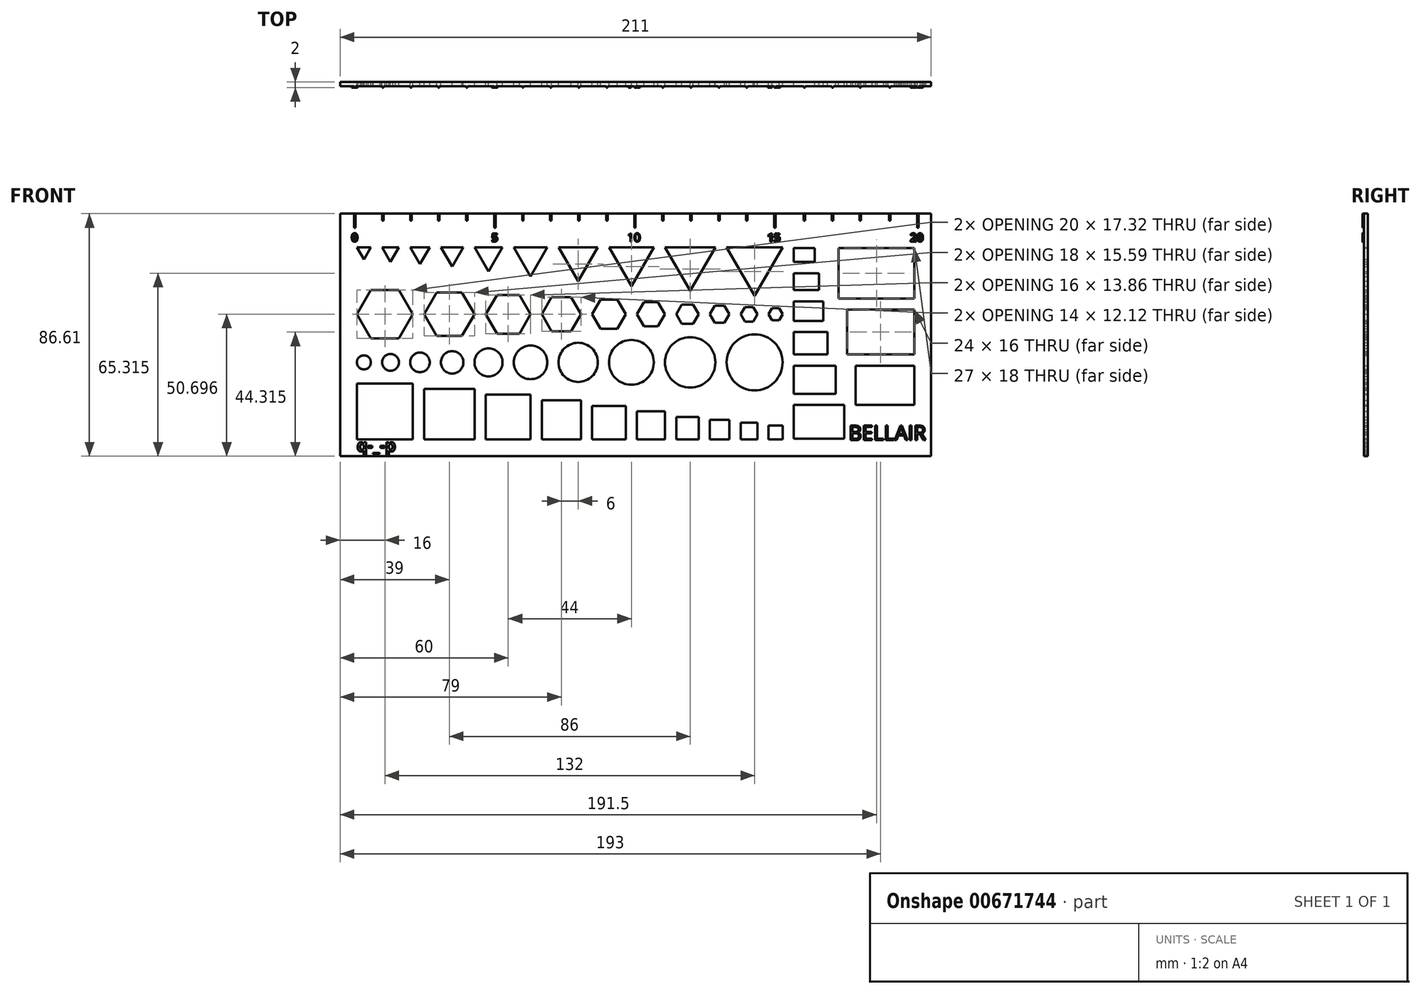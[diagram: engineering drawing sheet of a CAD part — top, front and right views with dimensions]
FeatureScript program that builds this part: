
annotation { "Feature Type Name" : "Feature", "Feature Type Description" : "" }
export const myFeature = defineFeature(function(context is Context, id is Id, definition is map)
    precondition{}
    {
        {
            var Q0;
            Q0=qCreatedBy(makeId("Front.planeOp"),FACE);
            var sketch = newSketch(context, id + "F0", { "sketchPlane" : qUnion([Q0])});
            skLineSegment(sketch, "E0.bottom", {"start": v(0, 0) * mm, "end": v(20, 0) * mm});
            skLineSegment(sketch, "E0.top", {"start": v(0, 20) * mm, "end": v(20, 20) * mm});
            skLineSegment(sketch, "E0.left", {"start": v(0, 0) * mm, "end": v(0, 20) * mm});
            skLineSegment(sketch, "E0.right", {"start": v(20, 0) * mm, "end": v(20, 20) * mm});
            skLineSegment(sketch, "E1.bottom", {"start": v(24, 0) * mm, "end": v(42, 0) * mm});
            skLineSegment(sketch, "E1.top", {"start": v(24, 18) * mm, "end": v(42, 18) * mm});
            skLineSegment(sketch, "E1.left", {"start": v(24, 0) * mm, "end": v(24, 18) * mm});
            skLineSegment(sketch, "E1.right", {"start": v(42, 0) * mm, "end": v(42, 18) * mm});
            skLineSegment(sketch, "E2.bottom", {"start": v(46, 0) * mm, "end": v(62, 0) * mm});
            skLineSegment(sketch, "E2.top", {"start": v(46, 16) * mm, "end": v(62, 16) * mm});
            skLineSegment(sketch, "E2.left", {"start": v(46, 0) * mm, "end": v(46, 16) * mm});
            skLineSegment(sketch, "E2.right", {"start": v(62, 0) * mm, "end": v(62, 16) * mm});
            skLineSegment(sketch, "E3.bottom", {"start": v(66, 0) * mm, "end": v(80, 0) * mm});
            skLineSegment(sketch, "E3.top", {"start": v(66, 14) * mm, "end": v(80, 14) * mm});
            skLineSegment(sketch, "E3.left", {"start": v(66, 0) * mm, "end": v(66, 14) * mm});
            skLineSegment(sketch, "E3.right", {"start": v(80, 0) * mm, "end": v(80, 14) * mm});
            skLineSegment(sketch, "E4.bottom", {"start": v(84, 0) * mm, "end": v(96, 0) * mm});
            skLineSegment(sketch, "E4.top", {"start": v(84, 12) * mm, "end": v(96, 12) * mm});
            skLineSegment(sketch, "E4.left", {"start": v(84, 0) * mm, "end": v(84, 12) * mm});
            skLineSegment(sketch, "E4.right", {"start": v(96, 0) * mm, "end": v(96, 12) * mm});
            skLineSegment(sketch, "E5.bottom", {"start": v(100, 0) * mm, "end": v(110, 0) * mm});
            skLineSegment(sketch, "E5.top", {"start": v(100, 10) * mm, "end": v(110, 10) * mm});
            skLineSegment(sketch, "E5.left", {"start": v(100, 0) * mm, "end": v(100, 10) * mm});
            skLineSegment(sketch, "E5.right", {"start": v(110, 0) * mm, "end": v(110, 10) * mm});
            skLineSegment(sketch, "E6.bottom", {"start": v(114, 0) * mm, "end": v(122, 0) * mm});
            skLineSegment(sketch, "E6.top", {"start": v(114, 8) * mm, "end": v(122, 8) * mm});
            skLineSegment(sketch, "E6.left", {"start": v(114, 0) * mm, "end": v(114, 8) * mm});
            skLineSegment(sketch, "E6.right", {"start": v(122, 0) * mm, "end": v(122, 8) * mm});
            skLineSegment(sketch, "E7.bottom", {"start": v(126, 0) * mm, "end": v(133, 0) * mm});
            skLineSegment(sketch, "E7.top", {"start": v(126, 7) * mm, "end": v(133, 7) * mm});
            skLineSegment(sketch, "E7.left", {"start": v(126, 0) * mm, "end": v(126, 7) * mm});
            skLineSegment(sketch, "E7.right", {"start": v(133, 0) * mm, "end": v(133, 7) * mm});
            skLineSegment(sketch, "E8.bottom", {"start": v(137, 0) * mm, "end": v(143, 0) * mm});
            skLineSegment(sketch, "E8.top", {"start": v(137, 6) * mm, "end": v(143, 6) * mm});
            skLineSegment(sketch, "E8.left", {"start": v(137, 0) * mm, "end": v(137, 6) * mm});
            skLineSegment(sketch, "E8.right", {"start": v(143, 0) * mm, "end": v(143, 6) * mm});
            skLineSegment(sketch, "E9.bottom", {"start": v(147, 0) * mm, "end": v(152, 0) * mm});
            skLineSegment(sketch, "E9.top", {"start": v(147, 5) * mm, "end": v(152, 5) * mm});
            skLineSegment(sketch, "E9.left", {"start": v(147, 0) * mm, "end": v(147, 5) * mm});
            skLineSegment(sketch, "E9.right", {"start": v(152, 0) * mm, "end": v(152, 5) * mm});
            skCircle(sketch, "E10", {"center": v(2.5, 27.5) * mm, "radius": 2.5 * mm});
            skCircle(sketch, "E11", {"center": v(12, 27.5) * mm, "radius": 3 * mm});
            skCircle(sketch, "E12", {"center": v(22.5, 27.5) * mm, "radius": 3.5 * mm});
            skCircle(sketch, "E13", {"center": v(34, 27.5) * mm, "radius": 4 * mm});
            skCircle(sketch, "E14", {"center": v(47, 27.5) * mm, "radius": 5 * mm});
            skCircle(sketch, "E15", {"center": v(62, 27.5) * mm, "radius": 6 * mm});
            skCircle(sketch, "E16", {"center": v(79, 27.5) * mm, "radius": 7 * mm});
            skCircle(sketch, "E17", {"center": v(98, 27.5) * mm, "radius": 8 * mm});
            skCircle(sketch, "E18", {"center": v(119, 27.5) * mm, "radius": 9 * mm});
            skCircle(sketch, "E19", {"center": v(142, 27.5) * mm, "radius": 10 * mm});
            skCircle(sketch, "E20.cCircle", {"center": v(10, 44.7) * mm, "radius": 8.66 * mm, "construction": true});
            skLineSegment(sketch, "E20.0", {"start": v(5, 53.36) * mm, "end": v(15, 53.36) * mm});
            skLineSegment(sketch, "E20.1", {"start": v(15, 53.36) * mm, "end": v(20, 44.7) * mm});
            skLineSegment(sketch, "E20.2", {"start": v(20, 44.7) * mm, "end": v(15, 36.04) * mm});
            skLineSegment(sketch, "E20.3", {"start": v(15, 36.04) * mm, "end": v(5, 36.04) * mm});
            skLineSegment(sketch, "E20.4", {"start": v(5, 36.04) * mm, "end": v(0, 44.7) * mm});
            skLineSegment(sketch, "E20.5", {"start": v(0, 44.7) * mm, "end": v(5, 53.36) * mm});
            skPoint(sketch, "E20.0.midPoint", {"position": v(10, 53.36) * mm});
            skCircle(sketch, "E21.cCircle", {"center": v(33, 44.7) * mm, "radius": 7.8 * mm, "construction": true});
            skLineSegment(sketch, "E21.0", {"start": v(37.5, 36.9) * mm, "end": v(28.5, 36.9) * mm});
            skLineSegment(sketch, "E21.1", {"start": v(28.5, 36.9) * mm, "end": v(24, 44.7) * mm});
            skLineSegment(sketch, "E21.2", {"start": v(24, 44.7) * mm, "end": v(28.5, 52.5) * mm});
            skLineSegment(sketch, "E21.3", {"start": v(28.5, 52.5) * mm, "end": v(37.5, 52.5) * mm});
            skLineSegment(sketch, "E21.4", {"start": v(37.5, 52.5) * mm, "end": v(42, 44.7) * mm});
            skLineSegment(sketch, "E21.5", {"start": v(42, 44.7) * mm, "end": v(37.5, 36.9) * mm});
            skPoint(sketch, "E21.0.midPoint", {"position": v(33, 36.9) * mm});
            skCircle(sketch, "E22.cCircle", {"center": v(54, 44.7) * mm, "radius": 6.93 * mm, "construction": true});
            skLineSegment(sketch, "E22.0", {"start": v(50, 51.62) * mm, "end": v(58, 51.62) * mm});
            skLineSegment(sketch, "E22.1", {"start": v(58, 51.62) * mm, "end": v(62, 44.7) * mm});
            skLineSegment(sketch, "E22.2", {"start": v(62, 44.7) * mm, "end": v(58, 37.77) * mm});
            skLineSegment(sketch, "E22.3", {"start": v(58, 37.77) * mm, "end": v(50, 37.77) * mm});
            skLineSegment(sketch, "E22.4", {"start": v(50, 37.77) * mm, "end": v(46, 44.7) * mm});
            skLineSegment(sketch, "E22.5", {"start": v(46, 44.7) * mm, "end": v(50, 51.62) * mm});
            skPoint(sketch, "E22.0.midPoint", {"position": v(54, 51.62) * mm});
            skCircle(sketch, "E23.cCircle", {"center": v(73, 44.7) * mm, "radius": 6.06 * mm, "construction": true});
            skLineSegment(sketch, "E23.0", {"start": v(69.5, 50.76) * mm, "end": v(76.5, 50.76) * mm});
            skLineSegment(sketch, "E23.1", {"start": v(76.5, 50.76) * mm, "end": v(80, 44.7) * mm});
            skLineSegment(sketch, "E23.2", {"start": v(80, 44.7) * mm, "end": v(76.5, 38.63) * mm});
            skLineSegment(sketch, "E23.3", {"start": v(76.5, 38.63) * mm, "end": v(69.5, 38.63) * mm});
            skLineSegment(sketch, "E23.4", {"start": v(69.5, 38.63) * mm, "end": v(66, 44.7) * mm});
            skLineSegment(sketch, "E23.5", {"start": v(66, 44.7) * mm, "end": v(69.5, 50.76) * mm});
            skPoint(sketch, "E23.0.midPoint", {"position": v(73, 50.76) * mm});
            skCircle(sketch, "E24.cCircle", {"center": v(90, 44.7) * mm, "radius": 5.2 * mm, "construction": true});
            skLineSegment(sketch, "E24.0", {"start": v(87, 49.9) * mm, "end": v(93, 49.9) * mm});
            skLineSegment(sketch, "E24.1", {"start": v(93, 49.9) * mm, "end": v(96, 44.7) * mm});
            skLineSegment(sketch, "E24.2", {"start": v(96, 44.7) * mm, "end": v(93, 39.5) * mm});
            skLineSegment(sketch, "E24.3", {"start": v(93, 39.5) * mm, "end": v(87, 39.5) * mm});
            skLineSegment(sketch, "E24.4", {"start": v(87, 39.5) * mm, "end": v(84, 44.7) * mm});
            skLineSegment(sketch, "E24.5", {"start": v(84, 44.7) * mm, "end": v(87, 49.9) * mm});
            skPoint(sketch, "E24.0.midPoint", {"position": v(90, 49.9) * mm});
            skCircle(sketch, "E25.cCircle", {"center": v(105, 44.7) * mm, "radius": 4.33 * mm, "construction": true});
            skLineSegment(sketch, "E25.0", {"start": v(102.5, 49.03) * mm, "end": v(107.5, 49.03) * mm});
            skLineSegment(sketch, "E25.1", {"start": v(107.5, 49.03) * mm, "end": v(110, 44.7) * mm});
            skLineSegment(sketch, "E25.2", {"start": v(110, 44.7) * mm, "end": v(107.5, 40.37) * mm});
            skLineSegment(sketch, "E25.3", {"start": v(107.5, 40.37) * mm, "end": v(102.5, 40.37) * mm});
            skLineSegment(sketch, "E25.4", {"start": v(102.5, 40.37) * mm, "end": v(100, 44.7) * mm});
            skLineSegment(sketch, "E25.5", {"start": v(100, 44.7) * mm, "end": v(102.5, 49.03) * mm});
            skPoint(sketch, "E25.0.midPoint", {"position": v(105, 49.03) * mm});
            skCircle(sketch, "E26.cCircle", {"center": v(118, 44.7) * mm, "radius": 3.46 * mm, "construction": true});
            skLineSegment(sketch, "E26.0", {"start": v(116, 48.16) * mm, "end": v(120, 48.16) * mm});
            skLineSegment(sketch, "E26.1", {"start": v(120, 48.16) * mm, "end": v(122, 44.7) * mm});
            skLineSegment(sketch, "E26.2", {"start": v(122, 44.7) * mm, "end": v(120, 41.23) * mm});
            skLineSegment(sketch, "E26.3", {"start": v(120, 41.23) * mm, "end": v(116, 41.23) * mm});
            skLineSegment(sketch, "E26.4", {"start": v(116, 41.23) * mm, "end": v(114, 44.7) * mm});
            skLineSegment(sketch, "E26.5", {"start": v(114, 44.7) * mm, "end": v(116, 48.16) * mm});
            skPoint(sketch, "E26.0.midPoint", {"position": v(118, 48.16) * mm});
            skCircle(sketch, "E27.cCircle", {"center": v(129.5, 44.7) * mm, "radius": 3.03 * mm, "construction": true});
            skLineSegment(sketch, "E27.0", {"start": v(127.75, 47.73) * mm, "end": v(131.25, 47.73) * mm});
            skLineSegment(sketch, "E27.1", {"start": v(131.25, 47.73) * mm, "end": v(133, 44.7) * mm});
            skLineSegment(sketch, "E27.2", {"start": v(133, 44.7) * mm, "end": v(131.25, 41.67) * mm});
            skLineSegment(sketch, "E27.3", {"start": v(131.25, 41.67) * mm, "end": v(127.75, 41.67) * mm});
            skLineSegment(sketch, "E27.4", {"start": v(127.75, 41.67) * mm, "end": v(126, 44.7) * mm});
            skLineSegment(sketch, "E27.5", {"start": v(126, 44.7) * mm, "end": v(127.75, 47.73) * mm});
            skPoint(sketch, "E27.0.midPoint", {"position": v(129.5, 47.73) * mm});
            skCircle(sketch, "E28.cCircle", {"center": v(140, 44.7) * mm, "radius": 2.6 * mm, "construction": true});
            skLineSegment(sketch, "E28.0", {"start": v(138.5, 47.3) * mm, "end": v(141.5, 47.3) * mm});
            skLineSegment(sketch, "E28.1", {"start": v(141.5, 47.3) * mm, "end": v(143, 44.7) * mm});
            skLineSegment(sketch, "E28.2", {"start": v(143, 44.7) * mm, "end": v(141.5, 42.1) * mm});
            skLineSegment(sketch, "E28.3", {"start": v(141.5, 42.1) * mm, "end": v(138.5, 42.1) * mm});
            skLineSegment(sketch, "E28.4", {"start": v(138.5, 42.1) * mm, "end": v(137, 44.7) * mm});
            skLineSegment(sketch, "E28.5", {"start": v(137, 44.7) * mm, "end": v(138.5, 47.3) * mm});
            skPoint(sketch, "E28.0.midPoint", {"position": v(140, 47.3) * mm});
            skCircle(sketch, "E29.cCircle", {"center": v(149.5, 44.7) * mm, "radius": 2.17 * mm, "construction": true});
            skLineSegment(sketch, "E29.0", {"start": v(148.25, 46.86) * mm, "end": v(150.75, 46.86) * mm});
            skLineSegment(sketch, "E29.1", {"start": v(150.75, 46.86) * mm, "end": v(152, 44.7) * mm});
            skLineSegment(sketch, "E29.2", {"start": v(152, 44.7) * mm, "end": v(150.75, 42.53) * mm});
            skLineSegment(sketch, "E29.3", {"start": v(150.75, 42.53) * mm, "end": v(148.25, 42.53) * mm});
            skLineSegment(sketch, "E29.4", {"start": v(148.25, 42.53) * mm, "end": v(147, 44.7) * mm});
            skLineSegment(sketch, "E29.5", {"start": v(147, 44.7) * mm, "end": v(148.25, 46.86) * mm});
            skPoint(sketch, "E29.0.midPoint", {"position": v(149.5, 46.86) * mm});
            skCircle(sketch, "E30.cCircle", {"center": v(2.5, 67.17) * mm, "radius": 1.44 * mm, "construction": true});
            skLineSegment(sketch, "E30.0", {"start": v(0, 68.61) * mm, "end": v(5, 68.61) * mm});
            skLineSegment(sketch, "E30.1", {"start": v(5, 68.61) * mm, "end": v(2.5, 64.28) * mm});
            skLineSegment(sketch, "E30.2", {"start": v(2.5, 64.28) * mm, "end": v(0, 68.61) * mm});
            skPoint(sketch, "E30.0.midPoint", {"position": v(2.5, 68.61) * mm});
            skCircle(sketch, "E31.cCircle", {"center": v(12, 66.88) * mm, "radius": 1.73 * mm, "construction": true});
            skLineSegment(sketch, "E31.0", {"start": v(9, 68.61) * mm, "end": v(15, 68.61) * mm});
            skLineSegment(sketch, "E31.1", {"start": v(15, 68.61) * mm, "end": v(12, 63.42) * mm});
            skLineSegment(sketch, "E31.2", {"start": v(12, 63.42) * mm, "end": v(9, 68.61) * mm});
            skPoint(sketch, "E31.0.midPoint", {"position": v(12, 68.61) * mm});
            skCircle(sketch, "E32.cCircle", {"center": v(22.5, 66.6) * mm, "radius": 2.02 * mm, "construction": true});
            skLineSegment(sketch, "E32.0", {"start": v(19, 68.61) * mm, "end": v(26, 68.61) * mm});
            skLineSegment(sketch, "E32.1", {"start": v(26, 68.61) * mm, "end": v(22.5, 62.55) * mm});
            skLineSegment(sketch, "E32.2", {"start": v(22.5, 62.55) * mm, "end": v(19, 68.61) * mm});
            skPoint(sketch, "E32.0.midPoint", {"position": v(22.5, 68.61) * mm});
            skCircle(sketch, "E33.cCircle", {"center": v(34, 66.3) * mm, "radius": 2.3 * mm, "construction": true});
            skLineSegment(sketch, "E33.0", {"start": v(30, 68.61) * mm, "end": v(38, 68.61) * mm});
            skLineSegment(sketch, "E33.1", {"start": v(38, 68.61) * mm, "end": v(34, 61.69) * mm});
            skLineSegment(sketch, "E33.2", {"start": v(34, 61.69) * mm, "end": v(30, 68.61) * mm});
            skPoint(sketch, "E33.0.midPoint", {"position": v(34, 68.61) * mm});
            skCircle(sketch, "E34.cCircle", {"center": v(47, 65.73) * mm, "radius": 2.89 * mm, "construction": true});
            skLineSegment(sketch, "E34.0", {"start": v(42, 68.61) * mm, "end": v(52, 68.61) * mm});
            skLineSegment(sketch, "E34.1", {"start": v(52, 68.61) * mm, "end": v(47, 59.95) * mm});
            skLineSegment(sketch, "E34.2", {"start": v(47, 59.95) * mm, "end": v(42, 68.61) * mm});
            skPoint(sketch, "E34.0.midPoint", {"position": v(47, 68.61) * mm});
            skCircle(sketch, "E35.cCircle", {"center": v(79, 64.57) * mm, "radius": 4.04 * mm, "construction": true});
            skLineSegment(sketch, "E35.0", {"start": v(72, 68.61) * mm, "end": v(86, 68.61) * mm});
            skLineSegment(sketch, "E35.1", {"start": v(86, 68.61) * mm, "end": v(79, 56.5) * mm});
            skLineSegment(sketch, "E35.2", {"start": v(79, 56.5) * mm, "end": v(72, 68.61) * mm});
            skPoint(sketch, "E35.0.midPoint", {"position": v(79, 68.61) * mm});
            skCircle(sketch, "E36.cCircle", {"center": v(98, 64) * mm, "radius": 4.62 * mm, "construction": true});
            skLineSegment(sketch, "E36.0", {"start": v(90, 68.61) * mm, "end": v(106, 68.61) * mm});
            skLineSegment(sketch, "E36.1", {"start": v(106, 68.61) * mm, "end": v(98, 54.76) * mm});
            skLineSegment(sketch, "E36.2", {"start": v(98, 54.76) * mm, "end": v(90, 68.61) * mm});
            skPoint(sketch, "E36.0.midPoint", {"position": v(98, 68.61) * mm});
            skCircle(sketch, "E37.cCircle", {"center": v(119, 63.42) * mm, "radius": 5.2 * mm, "construction": true});
            skLineSegment(sketch, "E37.0", {"start": v(110, 68.61) * mm, "end": v(128, 68.61) * mm});
            skLineSegment(sketch, "E37.1", {"start": v(128, 68.61) * mm, "end": v(119, 53.03) * mm});
            skLineSegment(sketch, "E37.2", {"start": v(119, 53.03) * mm, "end": v(110, 68.61) * mm});
            skPoint(sketch, "E37.0.midPoint", {"position": v(119, 68.61) * mm});
            skCircle(sketch, "E38.cCircle", {"center": v(62, 65.15) * mm, "radius": 3.46 * mm, "construction": true});
            skLineSegment(sketch, "E38.0", {"start": v(56, 68.61) * mm, "end": v(68, 68.61) * mm});
            skLineSegment(sketch, "E38.1", {"start": v(68, 68.61) * mm, "end": v(62, 58.22) * mm});
            skLineSegment(sketch, "E38.2", {"start": v(62, 58.22) * mm, "end": v(56, 68.61) * mm});
            skPoint(sketch, "E38.0.midPoint", {"position": v(62, 68.61) * mm});
            skCircle(sketch, "E39.cCircle", {"center": v(142, 62.84) * mm, "radius": 5.77 * mm, "construction": true});
            skLineSegment(sketch, "E39.0", {"start": v(132, 68.61) * mm, "end": v(152, 68.61) * mm});
            skLineSegment(sketch, "E39.1", {"start": v(152, 68.61) * mm, "end": v(142, 51.3) * mm});
            skLineSegment(sketch, "E39.2", {"start": v(142, 51.3) * mm, "end": v(132, 68.61) * mm});
            skPoint(sketch, "E39.0.midPoint", {"position": v(142, 68.61) * mm});
            skLineSegment(sketch, "E40", {"start": v(156, 68.61) * mm, "end": v(156, 0) * mm});
            skLineSegment(sketch, "E41.bottom", {"start": v(156, 68.31) * mm, "end": v(163.5, 68.31) * mm});
            skLineSegment(sketch, "E41.top", {"start": v(156, 63.31) * mm, "end": v(163.5, 63.31) * mm});
            skLineSegment(sketch, "E41.left", {"start": v(156, 68.31) * mm, "end": v(156, 63.31) * mm});
            skLineSegment(sketch, "E41.right", {"start": v(163.5, 68.31) * mm, "end": v(163.5, 63.31) * mm});
            skLineSegment(sketch, "E42.bottom", {"start": v(156, 59.31) * mm, "end": v(165, 59.31) * mm});
            skLineSegment(sketch, "E42.top", {"start": v(156, 53.31) * mm, "end": v(165, 53.31) * mm});
            skLineSegment(sketch, "E42.left", {"start": v(156, 59.31) * mm, "end": v(156, 53.31) * mm});
            skLineSegment(sketch, "E42.right", {"start": v(165, 59.31) * mm, "end": v(165, 53.31) * mm});
            skLineSegment(sketch, "E43.bottom", {"start": v(156, 49.31) * mm, "end": v(166.5, 49.31) * mm});
            skLineSegment(sketch, "E43.top", {"start": v(156, 42.31) * mm, "end": v(166.5, 42.31) * mm});
            skLineSegment(sketch, "E43.left", {"start": v(156, 49.31) * mm, "end": v(156, 42.31) * mm});
            skLineSegment(sketch, "E43.right", {"start": v(166.5, 49.31) * mm, "end": v(166.5, 42.31) * mm});
            skLineSegment(sketch, "E44.bottom", {"start": v(156, 38.31) * mm, "end": v(168, 38.31) * mm});
            skLineSegment(sketch, "E44.top", {"start": v(156, 30.31) * mm, "end": v(168, 30.31) * mm});
            skLineSegment(sketch, "E44.left", {"start": v(156, 38.31) * mm, "end": v(156, 30.31) * mm});
            skLineSegment(sketch, "E44.right", {"start": v(168, 38.31) * mm, "end": v(168, 30.31) * mm});
            skLineSegment(sketch, "E45.bottom", {"start": v(156, 26.31) * mm, "end": v(171, 26.31) * mm});
            skLineSegment(sketch, "E45.top", {"start": v(156, 16.31) * mm, "end": v(171, 16.31) * mm});
            skLineSegment(sketch, "E45.left", {"start": v(156, 26.31) * mm, "end": v(156, 16.31) * mm});
            skLineSegment(sketch, "E45.right", {"start": v(171, 26.31) * mm, "end": v(171, 16.31) * mm});
            skLineSegment(sketch, "E46.bottom", {"start": v(156, 12.31) * mm, "end": v(174, 12.31) * mm});
            skLineSegment(sketch, "E46.top", {"start": v(156, 0.31) * mm, "end": v(174, 0.31) * mm});
            skLineSegment(sketch, "E46.left", {"start": v(156, 12.31) * mm, "end": v(156, 0.31) * mm});
            skLineSegment(sketch, "E46.right", {"start": v(174, 12.31) * mm, "end": v(174, 0.31) * mm});
            skLineSegment(sketch, "E47.bottom", {"start": v(199, 68.31) * mm, "end": v(172, 68.31) * mm});
            skLineSegment(sketch, "E47.top", {"start": v(199, 50.31) * mm, "end": v(172, 50.31) * mm});
            skLineSegment(sketch, "E47.left", {"start": v(199, 68.31) * mm, "end": v(199, 50.31) * mm});
            skLineSegment(sketch, "E47.right", {"start": v(172, 68.31) * mm, "end": v(172, 50.31) * mm});
            skLineSegment(sketch, "E48.bottom", {"start": v(199, 46.31) * mm, "end": v(175, 46.31) * mm});
            skLineSegment(sketch, "E48.top", {"start": v(199, 30.31) * mm, "end": v(175, 30.31) * mm});
            skLineSegment(sketch, "E48.left", {"start": v(199, 46.31) * mm, "end": v(199, 30.31) * mm});
            skLineSegment(sketch, "E48.right", {"start": v(175, 46.31) * mm, "end": v(175, 30.31) * mm});
            skLineSegment(sketch, "E49.bottom", {"start": v(199, 26.31) * mm, "end": v(178, 26.31) * mm});
            skLineSegment(sketch, "E49.top", {"start": v(199, 12.31) * mm, "end": v(178, 12.31) * mm});
            skLineSegment(sketch, "E49.left", {"start": v(199, 26.31) * mm, "end": v(199, 12.31) * mm});
            skLineSegment(sketch, "E49.right", {"start": v(178, 26.31) * mm, "end": v(178, 12.31) * mm});
            skLineSegment(sketch, "E50.bottom", {"start": v(-6, 80.61) * mm, "end": v(205, 80.61) * mm});
            skLineSegment(sketch, "E50.top", {"start": v(-6, -6) * mm, "end": v(205, -6) * mm});
            skLineSegment(sketch, "E50.left", {"start": v(-6, 80.61) * mm, "end": v(-6, -6) * mm});
            skLineSegment(sketch, "E50.right", {"start": v(205, 80.61) * mm, "end": v(205, -6) * mm});
            skSolve(sketch);
        }
        {
            var Q0;
            Q0 = qSketchRegion(id + "F0", true);
            extrude(context, id + "F1", {"entities" : qUnion([Q0]), "depth" : 1.5 * mm, "offsetDistance" : 25 * mm});
        }
        {
            var Q0;
            Q0=makeQuery(id+"F1.opExtrude","CAP_FACE",FACE,{"disambiguationData":[OSD([sQuery(id+"F0.wireOp",EDGE,"E0.bottom"),sQuery(id+"F0.wireOp",EDGE,"E0.top"),sQuery(id+"F0.wireOp",EDGE,"E0.left"),sQuery(id+"F0.wireOp",EDGE,"E0.right"),sQuery(id+"F0.wireOp",EDGE,"E1.bottom"),sQuery(id+"F0.wireOp",EDGE,"E1.top"),sQuery(id+"F0.wireOp",EDGE,"E1.left"),sQuery(id+"F0.wireOp",EDGE,"E1.right"),sQuery(id+"F0.wireOp",EDGE,"E2.bottom"),sQuery(id+"F0.wireOp",EDGE,"E2.top"),sQuery(id+"F0.wireOp",EDGE,"E2.left"),sQuery(id+"F0.wireOp",EDGE,"E2.right"),sQuery(id+"F0.wireOp",EDGE,"E3.bottom"),sQuery(id+"F0.wireOp",EDGE,"E3.top"),sQuery(id+"F0.wireOp",EDGE,"E3.left"),sQuery(id+"F0.wireOp",EDGE,"E3.right"),sQuery(id+"F0.wireOp",EDGE,"E4.bottom"),sQuery(id+"F0.wireOp",EDGE,"E4.top"),sQuery(id+"F0.wireOp",EDGE,"E4.left"),sQuery(id+"F0.wireOp",EDGE,"E4.right"),sQuery(id+"F0.wireOp",EDGE,"E5.bottom"),sQuery(id+"F0.wireOp",EDGE,"E5.top"),sQuery(id+"F0.wireOp",EDGE,"E5.left"),sQuery(id+"F0.wireOp",EDGE,"E5.right"),sQuery(id+"F0.wireOp",EDGE,"E6.bottom"),sQuery(id+"F0.wireOp",EDGE,"E6.top"),sQuery(id+"F0.wireOp",EDGE,"E6.left"),sQuery(id+"F0.wireOp",EDGE,"E6.right"),sQuery(id+"F0.wireOp",EDGE,"E7.bottom"),sQuery(id+"F0.wireOp",EDGE,"E7.top"),sQuery(id+"F0.wireOp",EDGE,"E7.left"),sQuery(id+"F0.wireOp",EDGE,"E7.right"),sQuery(id+"F0.wireOp",EDGE,"E8.bottom"),sQuery(id+"F0.wireOp",EDGE,"E8.top"),sQuery(id+"F0.wireOp",EDGE,"E8.left"),sQuery(id+"F0.wireOp",EDGE,"E8.right"),sQuery(id+"F0.wireOp",EDGE,"E9.bottom"),sQuery(id+"F0.wireOp",EDGE,"E9.top"),sQuery(id+"F0.wireOp",EDGE,"E9.left"),sQuery(id+"F0.wireOp",EDGE,"E9.right"),sQuery(id+"F0.wireOp",EDGE,"E10"),sQuery(id+"F0.wireOp",EDGE,"E11"),sQuery(id+"F0.wireOp",EDGE,"E12"),sQuery(id+"F0.wireOp",EDGE,"E13"),sQuery(id+"F0.wireOp",EDGE,"E14"),sQuery(id+"F0.wireOp",EDGE,"E15"),sQuery(id+"F0.wireOp",EDGE,"E16"),sQuery(id+"F0.wireOp",EDGE,"E17"),sQuery(id+"F0.wireOp",EDGE,"E18"),sQuery(id+"F0.wireOp",EDGE,"E19"),sQuery(id+"F0.wireOp",EDGE,"E20.0"),sQuery(id+"F0.wireOp",EDGE,"E20.1"),sQuery(id+"F0.wireOp",EDGE,"E20.2"),sQuery(id+"F0.wireOp",EDGE,"E20.3"),sQuery(id+"F0.wireOp",EDGE,"E20.4"),sQuery(id+"F0.wireOp",EDGE,"E20.5"),sQuery(id+"F0.wireOp",EDGE,"E21.0"),sQuery(id+"F0.wireOp",EDGE,"E21.1"),sQuery(id+"F0.wireOp",EDGE,"E21.2"),sQuery(id+"F0.wireOp",EDGE,"E21.3"),sQuery(id+"F0.wireOp",EDGE,"E21.4"),sQuery(id+"F0.wireOp",EDGE,"E21.5"),sQuery(id+"F0.wireOp",EDGE,"E22.0"),sQuery(id+"F0.wireOp",EDGE,"E22.1"),sQuery(id+"F0.wireOp",EDGE,"E22.2"),sQuery(id+"F0.wireOp",EDGE,"E22.3"),sQuery(id+"F0.wireOp",EDGE,"E22.4"),sQuery(id+"F0.wireOp",EDGE,"E22.5"),sQuery(id+"F0.wireOp",EDGE,"E23.0"),sQuery(id+"F0.wireOp",EDGE,"E23.1"),sQuery(id+"F0.wireOp",EDGE,"E23.2"),sQuery(id+"F0.wireOp",EDGE,"E23.3"),sQuery(id+"F0.wireOp",EDGE,"E23.4"),sQuery(id+"F0.wireOp",EDGE,"E23.5"),sQuery(id+"F0.wireOp",EDGE,"E24.0"),sQuery(id+"F0.wireOp",EDGE,"E24.1"),sQuery(id+"F0.wireOp",EDGE,"E24.2"),sQuery(id+"F0.wireOp",EDGE,"E24.3"),sQuery(id+"F0.wireOp",EDGE,"E24.4"),sQuery(id+"F0.wireOp",EDGE,"E24.5"),sQuery(id+"F0.wireOp",EDGE,"E25.0"),sQuery(id+"F0.wireOp",EDGE,"E25.1"),sQuery(id+"F0.wireOp",EDGE,"E25.2"),sQuery(id+"F0.wireOp",EDGE,"E25.3"),sQuery(id+"F0.wireOp",EDGE,"E25.4"),sQuery(id+"F0.wireOp",EDGE,"E25.5"),sQuery(id+"F0.wireOp",EDGE,"E26.0"),sQuery(id+"F0.wireOp",EDGE,"E26.1"),sQuery(id+"F0.wireOp",EDGE,"E26.2"),sQuery(id+"F0.wireOp",EDGE,"E26.3"),sQuery(id+"F0.wireOp",EDGE,"E26.4"),sQuery(id+"F0.wireOp",EDGE,"E26.5"),sQuery(id+"F0.wireOp",EDGE,"E27.0"),sQuery(id+"F0.wireOp",EDGE,"E27.1"),sQuery(id+"F0.wireOp",EDGE,"E27.2"),sQuery(id+"F0.wireOp",EDGE,"E27.3"),sQuery(id+"F0.wireOp",EDGE,"E27.4"),sQuery(id+"F0.wireOp",EDGE,"E27.5"),sQuery(id+"F0.wireOp",EDGE,"E28.0"),sQuery(id+"F0.wireOp",EDGE,"E28.1"),sQuery(id+"F0.wireOp",EDGE,"E28.2"),sQuery(id+"F0.wireOp",EDGE,"E28.3"),sQuery(id+"F0.wireOp",EDGE,"E28.4"),sQuery(id+"F0.wireOp",EDGE,"E28.5"),sQuery(id+"F0.wireOp",EDGE,"E29.0"),sQuery(id+"F0.wireOp",EDGE,"E29.1"),sQuery(id+"F0.wireOp",EDGE,"E29.2"),sQuery(id+"F0.wireOp",EDGE,"E29.3"),sQuery(id+"F0.wireOp",EDGE,"E29.4"),sQuery(id+"F0.wireOp",EDGE,"E29.5"),sQuery(id+"F0.wireOp",EDGE,"E30.0"),sQuery(id+"F0.wireOp",EDGE,"E30.1"),sQuery(id+"F0.wireOp",EDGE,"E30.2"),sQuery(id+"F0.wireOp",EDGE,"E31.0"),sQuery(id+"F0.wireOp",EDGE,"E31.1"),sQuery(id+"F0.wireOp",EDGE,"E31.2"),sQuery(id+"F0.wireOp",EDGE,"E32.0"),sQuery(id+"F0.wireOp",EDGE,"E32.1"),sQuery(id+"F0.wireOp",EDGE,"E32.2"),sQuery(id+"F0.wireOp",EDGE,"E33.0"),sQuery(id+"F0.wireOp",EDGE,"E33.1"),sQuery(id+"F0.wireOp",EDGE,"E33.2"),sQuery(id+"F0.wireOp",EDGE,"E34.0"),sQuery(id+"F0.wireOp",EDGE,"E34.1"),sQuery(id+"F0.wireOp",EDGE,"E34.2"),sQuery(id+"F0.wireOp",EDGE,"E35.0"),sQuery(id+"F0.wireOp",EDGE,"E35.1"),sQuery(id+"F0.wireOp",EDGE,"E35.2"),sQuery(id+"F0.wireOp",EDGE,"E36.0"),sQuery(id+"F0.wireOp",EDGE,"E36.1"),sQuery(id+"F0.wireOp",EDGE,"E36.2"),sQuery(id+"F0.wireOp",EDGE,"E37.0"),sQuery(id+"F0.wireOp",EDGE,"E37.1"),sQuery(id+"F0.wireOp",EDGE,"E37.2"),sQuery(id+"F0.wireOp",EDGE,"E38.0"),sQuery(id+"F0.wireOp",EDGE,"E38.1"),sQuery(id+"F0.wireOp",EDGE,"E38.2"),sQuery(id+"F0.wireOp",EDGE,"E39.0"),sQuery(id+"F0.wireOp",EDGE,"E39.1"),sQuery(id+"F0.wireOp",EDGE,"E39.2"),sQuery(id+"F0.wireOp",EDGE,"E41.bottom"),sQuery(id+"F0.wireOp",EDGE,"E41.top"),sQuery(id+"F0.wireOp",EDGE,"E41.left"),sQuery(id+"F0.wireOp",EDGE,"E41.right"),sQuery(id+"F0.wireOp",EDGE,"E42.bottom"),sQuery(id+"F0.wireOp",EDGE,"E42.top"),sQuery(id+"F0.wireOp",EDGE,"E42.left"),sQuery(id+"F0.wireOp",EDGE,"E42.right"),sQuery(id+"F0.wireOp",EDGE,"E43.bottom"),sQuery(id+"F0.wireOp",EDGE,"E43.top"),sQuery(id+"F0.wireOp",EDGE,"E43.left"),sQuery(id+"F0.wireOp",EDGE,"E43.right"),sQuery(id+"F0.wireOp",EDGE,"E44.bottom"),sQuery(id+"F0.wireOp",EDGE,"E44.top"),sQuery(id+"F0.wireOp",EDGE,"E44.left"),sQuery(id+"F0.wireOp",EDGE,"E44.right"),sQuery(id+"F0.wireOp",EDGE,"E45.bottom"),sQuery(id+"F0.wireOp",EDGE,"E45.top"),sQuery(id+"F0.wireOp",EDGE,"E45.left"),sQuery(id+"F0.wireOp",EDGE,"E45.right"),sQuery(id+"F0.wireOp",EDGE,"E46.bottom"),sQuery(id+"F0.wireOp",EDGE,"E46.top"),sQuery(id+"F0.wireOp",EDGE,"E46.left"),sQuery(id+"F0.wireOp",EDGE,"E46.right"),sQuery(id+"F0.wireOp",EDGE,"E47.bottom"),sQuery(id+"F0.wireOp",EDGE,"E47.top"),sQuery(id+"F0.wireOp",EDGE,"E47.left"),sQuery(id+"F0.wireOp",EDGE,"E47.right"),sQuery(id+"F0.wireOp",EDGE,"E48.bottom"),sQuery(id+"F0.wireOp",EDGE,"E48.top"),sQuery(id+"F0.wireOp",EDGE,"E48.left"),sQuery(id+"F0.wireOp",EDGE,"E48.right"),sQuery(id+"F0.wireOp",EDGE,"E49.bottom"),sQuery(id+"F0.wireOp",EDGE,"E49.top"),sQuery(id+"F0.wireOp",EDGE,"E49.left"),sQuery(id+"F0.wireOp",EDGE,"E49.right"),sQuery(id+"F0.wireOp",EDGE,"E50.bottom"),sQuery(id+"F0.wireOp",EDGE,"E50.top"),sQuery(id+"F0.wireOp",EDGE,"E50.left"),sQuery(id+"F0.wireOp",EDGE,"E50.right")])],"isStart":false});
            var sketch = newSketch(context, id + "F2", { "sketchPlane" : qUnion([Q0])});
            skText(sketch, "E51", { "text": "BELLAIR", "fontName": "OpenSans-Regular.ttf"});
            const initialGuessF2  = {"E51": [0.17555, -0.00031, 1, 0, 0.00528]};
            skSetInitialGuess(sketch, initialGuessF2);
            skSolve(sketch);
        }
        {
            var Q0;
            Q0 = qSketchRegion(id + "F2", true);
            extrude(context, id + "F3", {"entities" : qUnion([Q0]), "operationType" : NewBodyOperationType.REMOVE, "oppositeDirection" : true, "depth" : 2 * mm, "offsetDistance" : 25 * mm});
        }
        {
            var Q0;
            {var subQ0=sQuery(id+"F0.wireOp",EDGE,"E50.right");var subQ1=sQuery(id+"F0.wireOp",EDGE,"E50.left");var subQ2=sQuery(id+"F0.wireOp",EDGE,"E50.top");var subQ3=sQuery(id+"F0.wireOp",EDGE,"E50.bottom");var subQ4=sQuery(id+"F0.wireOp",EDGE,"E49.right");var subQ5=sQuery(id+"F0.wireOp",EDGE,"E49.left");var subQ6=sQuery(id+"F0.wireOp",EDGE,"E49.top");var subQ7=sQuery(id+"F0.wireOp",EDGE,"E49.bottom");var subQ8=sQuery(id+"F0.wireOp",EDGE,"E48.right");var subQ9=sQuery(id+"F0.wireOp",EDGE,"E48.left");var subQ10=sQuery(id+"F0.wireOp",EDGE,"E48.top");var subQ11=sQuery(id+"F0.wireOp",EDGE,"E48.bottom");var subQ12=sQuery(id+"F0.wireOp",EDGE,"E47.right");var subQ13=sQuery(id+"F0.wireOp",EDGE,"E47.left");var subQ14=sQuery(id+"F0.wireOp",EDGE,"E47.top");var subQ15=sQuery(id+"F0.wireOp",EDGE,"E47.bottom");var subQ16=sQuery(id+"F0.wireOp",EDGE,"E46.right");var subQ17=sQuery(id+"F0.wireOp",EDGE,"E46.left");var subQ18=sQuery(id+"F0.wireOp",EDGE,"E46.top");var subQ19=sQuery(id+"F0.wireOp",EDGE,"E46.bottom");var subQ20=sQuery(id+"F0.wireOp",EDGE,"E45.right");var subQ21=sQuery(id+"F0.wireOp",EDGE,"E45.left");var subQ22=sQuery(id+"F0.wireOp",EDGE,"E45.top");var subQ23=sQuery(id+"F0.wireOp",EDGE,"E45.bottom");var subQ24=sQuery(id+"F0.wireOp",EDGE,"E44.right");var subQ25=sQuery(id+"F0.wireOp",EDGE,"E44.left");var subQ26=sQuery(id+"F0.wireOp",EDGE,"E44.top");var subQ27=sQuery(id+"F0.wireOp",EDGE,"E44.bottom");var subQ28=sQuery(id+"F0.wireOp",EDGE,"E43.right");var subQ29=sQuery(id+"F0.wireOp",EDGE,"E43.left");var subQ30=sQuery(id+"F0.wireOp",EDGE,"E43.top");var subQ31=sQuery(id+"F0.wireOp",EDGE,"E43.bottom");var subQ32=sQuery(id+"F0.wireOp",EDGE,"E42.right");var subQ33=sQuery(id+"F0.wireOp",EDGE,"E42.left");var subQ34=sQuery(id+"F0.wireOp",EDGE,"E42.top");var subQ35=sQuery(id+"F0.wireOp",EDGE,"E42.bottom");var subQ36=sQuery(id+"F0.wireOp",EDGE,"E41.right");var subQ37=sQuery(id+"F0.wireOp",EDGE,"E41.left");var subQ38=sQuery(id+"F0.wireOp",EDGE,"E41.top");var subQ39=sQuery(id+"F0.wireOp",EDGE,"E41.bottom");var subQ40=sQuery(id+"F0.wireOp",EDGE,"E39.2");var subQ41=sQuery(id+"F0.wireOp",EDGE,"E39.1");var subQ42=sQuery(id+"F0.wireOp",EDGE,"E39.0");var subQ43=sQuery(id+"F0.wireOp",EDGE,"E38.2");var subQ44=sQuery(id+"F0.wireOp",EDGE,"E38.1");var subQ45=sQuery(id+"F0.wireOp",EDGE,"E38.0");var subQ46=sQuery(id+"F0.wireOp",EDGE,"E37.2");var subQ47=sQuery(id+"F0.wireOp",EDGE,"E37.1");var subQ48=sQuery(id+"F0.wireOp",EDGE,"E37.0");var subQ49=sQuery(id+"F0.wireOp",EDGE,"E36.2");var subQ50=sQuery(id+"F0.wireOp",EDGE,"E36.1");var subQ51=sQuery(id+"F0.wireOp",EDGE,"E36.0");var subQ52=sQuery(id+"F0.wireOp",EDGE,"E35.2");var subQ53=sQuery(id+"F0.wireOp",EDGE,"E35.1");var subQ54=sQuery(id+"F0.wireOp",EDGE,"E35.0");var subQ55=sQuery(id+"F0.wireOp",EDGE,"E34.2");var subQ56=sQuery(id+"F0.wireOp",EDGE,"E34.1");var subQ57=sQuery(id+"F0.wireOp",EDGE,"E34.0");var subQ58=sQuery(id+"F0.wireOp",EDGE,"E33.2");var subQ59=sQuery(id+"F0.wireOp",EDGE,"E33.1");var subQ60=sQuery(id+"F0.wireOp",EDGE,"E33.0");var subQ61=sQuery(id+"F0.wireOp",EDGE,"E32.2");var subQ62=sQuery(id+"F0.wireOp",EDGE,"E32.1");var subQ63=sQuery(id+"F0.wireOp",EDGE,"E32.0");var subQ64=sQuery(id+"F0.wireOp",EDGE,"E31.2");var subQ65=sQuery(id+"F0.wireOp",EDGE,"E31.1");var subQ66=sQuery(id+"F0.wireOp",EDGE,"E31.0");var subQ67=sQuery(id+"F0.wireOp",EDGE,"E30.2");var subQ68=sQuery(id+"F0.wireOp",EDGE,"E30.1");var subQ69=sQuery(id+"F0.wireOp",EDGE,"E30.0");var subQ70=sQuery(id+"F0.wireOp",EDGE,"E29.5");var subQ71=sQuery(id+"F0.wireOp",EDGE,"E29.4");var subQ72=sQuery(id+"F0.wireOp",EDGE,"E29.3");var subQ73=sQuery(id+"F0.wireOp",EDGE,"E29.2");var subQ74=sQuery(id+"F0.wireOp",EDGE,"E29.1");var subQ75=sQuery(id+"F0.wireOp",EDGE,"E29.0");var subQ76=sQuery(id+"F0.wireOp",EDGE,"E28.5");var subQ77=sQuery(id+"F0.wireOp",EDGE,"E28.4");var subQ78=sQuery(id+"F0.wireOp",EDGE,"E28.3");var subQ79=sQuery(id+"F0.wireOp",EDGE,"E28.2");var subQ80=sQuery(id+"F0.wireOp",EDGE,"E28.1");var subQ81=sQuery(id+"F0.wireOp",EDGE,"E28.0");var subQ82=sQuery(id+"F0.wireOp",EDGE,"E27.5");var subQ83=sQuery(id+"F0.wireOp",EDGE,"E27.4");var subQ84=sQuery(id+"F0.wireOp",EDGE,"E14");var subQ85=sQuery(id+"F0.wireOp",EDGE,"E13");var subQ86=sQuery(id+"F0.wireOp",EDGE,"E12");var subQ87=sQuery(id+"F0.wireOp",EDGE,"E11");var subQ88=sQuery(id+"F0.wireOp",EDGE,"E10");var subQ89=sQuery(id+"F0.wireOp",EDGE,"E9.right");var subQ90=sQuery(id+"F0.wireOp",EDGE,"E9.left");var subQ91=sQuery(id+"F0.wireOp",EDGE,"E21.3");var subQ92=sQuery(id+"F0.wireOp",EDGE,"E9.top");var subQ93=sQuery(id+"F0.wireOp",EDGE,"E21.2");var subQ94=sQuery(id+"F0.wireOp",EDGE,"E9.bottom");var subQ95=sQuery(id+"F0.wireOp",EDGE,"E21.1");var subQ96=sQuery(id+"F0.wireOp",EDGE,"E8.right");var subQ97=sQuery(id+"F0.wireOp",EDGE,"E21.0");var subQ98=sQuery(id+"F0.wireOp",EDGE,"E8.left");var subQ99=sQuery(id+"F0.wireOp",EDGE,"E20.5");var subQ100=sQuery(id+"F0.wireOp",EDGE,"E8.top");var subQ101=sQuery(id+"F0.wireOp",EDGE,"E20.4");var subQ102=sQuery(id+"F0.wireOp",EDGE,"E8.bottom");var subQ103=sQuery(id+"F0.wireOp",EDGE,"E20.3");var subQ104=sQuery(id+"F0.wireOp",EDGE,"E7.right");var subQ105=sQuery(id+"F0.wireOp",EDGE,"E20.2");var subQ106=sQuery(id+"F0.wireOp",EDGE,"E7.left");var subQ107=sQuery(id+"F0.wireOp",EDGE,"E20.1");var subQ108=sQuery(id+"F0.wireOp",EDGE,"E7.top");var subQ109=sQuery(id+"F0.wireOp",EDGE,"E20.0");var subQ110=sQuery(id+"F0.wireOp",EDGE,"E7.bottom");var subQ111=sQuery(id+"F0.wireOp",EDGE,"E6.right");var subQ112=sQuery(id+"F0.wireOp",EDGE,"E6.left");var subQ113=sQuery(id+"F0.wireOp",EDGE,"E17");var subQ114=sQuery(id+"F0.wireOp",EDGE,"E6.top");var subQ115=sQuery(id+"F0.wireOp",EDGE,"E6.bottom");var subQ116=sQuery(id+"F0.wireOp",EDGE,"E5.right");var subQ117=sQuery(id+"F0.wireOp",EDGE,"E5.left");var subQ118=sQuery(id+"F0.wireOp",EDGE,"E2.bottom");var subQ119=sQuery(id+"F0.wireOp",EDGE,"E1.right");var subQ120=sQuery(id+"F0.wireOp",EDGE,"E1.left");var subQ121=sQuery(id+"F0.wireOp",EDGE,"E1.top");var subQ122=sQuery(id+"F0.wireOp",EDGE,"E1.bottom");var subQ123=sQuery(id+"F0.wireOp",EDGE,"E2.top");var subQ124=sQuery(id+"F0.wireOp",EDGE,"E15");var subQ125=sQuery(id+"F0.wireOp",EDGE,"E0.bottom");var subQ126=sQuery(id+"F0.wireOp",EDGE,"E27.3");var subQ127=sQuery(id+"F0.wireOp",EDGE,"E5.top");var subQ128=sQuery(id+"F0.wireOp",EDGE,"E0.right");var subQ129=sQuery(id+"F0.wireOp",EDGE,"E0.top");var subQ130=sQuery(id+"F0.wireOp",EDGE,"E0.left");var subQ131=sQuery(id+"F0.wireOp",EDGE,"E2.left");var subQ132=sQuery(id+"F0.wireOp",EDGE,"E2.right");var subQ133=sQuery(id+"F0.wireOp",EDGE,"E3.bottom");var subQ134=sQuery(id+"F0.wireOp",EDGE,"E3.top");var subQ135=sQuery(id+"F0.wireOp",EDGE,"E3.left");var subQ136=sQuery(id+"F0.wireOp",EDGE,"E3.right");var subQ137=sQuery(id+"F0.wireOp",EDGE,"E4.bottom");var subQ138=sQuery(id+"F0.wireOp",EDGE,"E4.top");var subQ139=sQuery(id+"F0.wireOp",EDGE,"E4.left");var subQ140=sQuery(id+"F0.wireOp",EDGE,"E4.right");var subQ141=sQuery(id+"F0.wireOp",EDGE,"E5.bottom");var subQ142=sQuery(id+"F0.wireOp",EDGE,"E16");var subQ143=sQuery(id+"F0.wireOp",EDGE,"E18");var subQ144=sQuery(id+"F0.wireOp",EDGE,"E19");var subQ145=sQuery(id+"F0.wireOp",EDGE,"E24.0");var subQ146=sQuery(id+"F0.wireOp",EDGE,"E24.3");var subQ147=sQuery(id+"F0.wireOp",EDGE,"E24.4");var subQ148=sQuery(id+"F0.wireOp",EDGE,"E24.5");var subQ149=sQuery(id+"F0.wireOp",EDGE,"E25.0");var subQ150=sQuery(id+"F0.wireOp",EDGE,"E25.1");var subQ151=sQuery(id+"F0.wireOp",EDGE,"E25.2");var subQ152=sQuery(id+"F0.wireOp",EDGE,"E21.4");var subQ153=sQuery(id+"F0.wireOp",EDGE,"E21.5");var subQ154=sQuery(id+"F0.wireOp",EDGE,"E22.0");var subQ155=sQuery(id+"F0.wireOp",EDGE,"E22.1");var subQ156=sQuery(id+"F0.wireOp",EDGE,"E22.2");var subQ157=sQuery(id+"F0.wireOp",EDGE,"E22.3");var subQ158=sQuery(id+"F0.wireOp",EDGE,"E22.4");var subQ159=sQuery(id+"F0.wireOp",EDGE,"E22.5");var subQ160=sQuery(id+"F0.wireOp",EDGE,"E23.0");var subQ161=sQuery(id+"F0.wireOp",EDGE,"E23.1");var subQ162=sQuery(id+"F0.wireOp",EDGE,"E23.2");var subQ163=sQuery(id+"F0.wireOp",EDGE,"E23.3");var subQ164=sQuery(id+"F0.wireOp",EDGE,"E23.4");var subQ165=sQuery(id+"F0.wireOp",EDGE,"E23.5");var subQ166=sQuery(id+"F0.wireOp",EDGE,"E24.1");var subQ167=sQuery(id+"F0.wireOp",EDGE,"E24.2");var subQ168=sQuery(id+"F0.wireOp",EDGE,"E25.3");var subQ169=sQuery(id+"F0.wireOp",EDGE,"E25.4");var subQ170=sQuery(id+"F0.wireOp",EDGE,"E25.5");var subQ171=sQuery(id+"F0.wireOp",EDGE,"E26.0");var subQ172=sQuery(id+"F0.wireOp",EDGE,"E26.1");var subQ173=sQuery(id+"F0.wireOp",EDGE,"E26.2");var subQ174=sQuery(id+"F0.wireOp",EDGE,"E26.3");var subQ175=sQuery(id+"F0.wireOp",EDGE,"E26.4");var subQ176=sQuery(id+"F0.wireOp",EDGE,"E26.5");var subQ177=sQuery(id+"F0.wireOp",EDGE,"E27.0");var subQ178=sQuery(id+"F0.wireOp",EDGE,"E27.1");var subQ179=sQuery(id+"F0.wireOp",EDGE,"E27.2");Q0=makeQuery(id+"F3.boolean.opBoolean","SPLIT",FACE,{"disambiguationData":[TD([makeQuery(id+"F1.opExtrude","SWEPT_FACE",FACE,{"disambiguationData":[OSD([subQ125])]})])],"derivedFrom":makeQuery(id+"F1.opExtrude","CAP_FACE",FACE,{"disambiguationData":[OSD([subQ125,subQ129,subQ130,subQ128,subQ122,subQ121,subQ120,subQ119,subQ118,subQ123,subQ131,subQ132,subQ133,subQ134,subQ135,subQ136,subQ137,subQ138,subQ139,subQ140,subQ141,subQ127,subQ117,subQ116,subQ115,subQ114,subQ112,subQ111,subQ110,subQ108,subQ106,subQ104,subQ102,subQ100,subQ98,subQ96,subQ94,subQ92,subQ90,subQ89,subQ88,subQ87,subQ86,subQ85,subQ84,subQ124,subQ142,subQ113,subQ143,subQ144,subQ109,subQ107,subQ105,subQ103,subQ101,subQ99,subQ97,subQ95,subQ93,subQ91,subQ152,subQ153,subQ154,subQ155,subQ156,subQ157,subQ158,subQ159,subQ160,subQ161,subQ162,subQ163,subQ164,subQ165,subQ145,subQ166,subQ167,subQ146,subQ147,subQ148,subQ149,subQ150,subQ151,subQ168,subQ169,subQ170,subQ171,subQ172,subQ173,subQ174,subQ175,subQ176,subQ177,subQ178,subQ179,subQ126,subQ83,subQ82,subQ81,subQ80,subQ79,subQ78,subQ77,subQ76,subQ75,subQ74,subQ73,subQ72,subQ71,subQ70,subQ69,subQ68,subQ67,subQ66,subQ65,subQ64,subQ63,subQ62,subQ61,subQ60,subQ59,subQ58,subQ57,subQ56,subQ55,subQ54,subQ53,subQ52,subQ51,subQ50,subQ49,subQ48,subQ47,subQ46,subQ45,subQ44,subQ43,subQ42,subQ41,subQ40,subQ39,subQ38,subQ37,subQ36,subQ35,subQ34,subQ33,subQ32,subQ31,subQ30,subQ29,subQ28,subQ27,subQ26,subQ25,subQ24,subQ23,subQ22,subQ21,subQ20,subQ19,subQ18,subQ17,subQ16,subQ15,subQ14,subQ13,subQ12,subQ11,subQ10,subQ9,subQ8,subQ7,subQ6,subQ5,subQ4,subQ3,subQ2,subQ1,subQ0])],"isStart":false})});}
            var sketch = newSketch(context, id + "F4", { "sketchPlane" : qUnion([Q0])});
            skText(sketch, "E52", { "text": "q-_-p", "fontName": "OpenSans-Bold.ttf"});
            const initialGuessF4  = {"E52": [0, -0.0043, 1, 0, 0.0043]};
            skSetInitialGuess(sketch, initialGuessF4);
            skSolve(sketch);
        }
        {
            var Q0;
            Q0 = qSketchRegion(id + "F4", true);
            extrude(context, id + "F5", {"entities" : qUnion([Q0]), "operationType" : NewBodyOperationType.REMOVE, "oppositeDirection" : true, "depth" : 2 * mm, "offsetDistance" : 25 * mm});
        }
        {
            var Q0;
            {var subQ0=sQuery(id+"F0.wireOp",EDGE,"E38.0");var subQ1=sQuery(id+"F0.wireOp",EDGE,"E37.2");var subQ2=sQuery(id+"F0.wireOp",EDGE,"E37.1");var subQ3=sQuery(id+"F0.wireOp",EDGE,"E37.0");var subQ4=sQuery(id+"F0.wireOp",EDGE,"E36.2");var subQ6=sQuery(id+"F0.wireOp",EDGE,"E36.1");var subQ8=sQuery(id+"F0.wireOp",EDGE,"E36.0");var subQ10=sQuery(id+"F0.wireOp",EDGE,"E35.2");var subQ11=sQuery(id+"F0.wireOp",EDGE,"E35.1");var subQ12=sQuery(id+"F0.wireOp",EDGE,"E35.0");var subQ13=sQuery(id+"F0.wireOp",EDGE,"E34.2");var subQ14=sQuery(id+"F0.wireOp",EDGE,"E34.1");var subQ15=sQuery(id+"F0.wireOp",EDGE,"E34.0");var subQ16=sQuery(id+"F0.wireOp",EDGE,"E33.2");var subQ17=sQuery(id+"F0.wireOp",EDGE,"E33.1");var subQ19=sQuery(id+"F0.wireOp",EDGE,"E33.0");var subQ21=sQuery(id+"F0.wireOp",EDGE,"E32.2");var subQ23=sQuery(id+"F0.wireOp",EDGE,"E32.1");var subQ25=sQuery(id+"F0.wireOp",EDGE,"E32.0");var subQ26=sQuery(id+"F0.wireOp",EDGE,"E31.2");var subQ28=sQuery(id+"F0.wireOp",EDGE,"E31.1");var subQ29=sQuery(id+"F0.wireOp",EDGE,"E31.0");var subQ30=sQuery(id+"F0.wireOp",EDGE,"E30.2");var subQ32=sQuery(id+"F0.wireOp",EDGE,"E30.1");var subQ34=sQuery(id+"F0.wireOp",EDGE,"E30.0");var subQ36=sQuery(id+"F0.wireOp",EDGE,"E29.5");var subQ38=sQuery(id+"F0.wireOp",EDGE,"E29.4");var subQ39=sQuery(id+"F0.wireOp",EDGE,"E29.3");var subQ41=sQuery(id+"F0.wireOp",EDGE,"E29.2");var subQ42=sQuery(id+"F0.wireOp",EDGE,"E29.1");var subQ44=sQuery(id+"F0.wireOp",EDGE,"E29.0");var subQ46=sQuery(id+"F0.wireOp",EDGE,"E28.5");var subQ48=sQuery(id+"F0.wireOp",EDGE,"E28.4");var subQ50=sQuery(id+"F0.wireOp",EDGE,"E28.3");var subQ52=sQuery(id+"F0.wireOp",EDGE,"E28.2");var subQ54=sQuery(id+"F0.wireOp",EDGE,"E28.1");var subQ56=sQuery(id+"F0.wireOp",EDGE,"E28.0");var subQ58=sQuery(id+"F0.wireOp",EDGE,"E27.5");var subQ60=sQuery(id+"F0.wireOp",EDGE,"E27.4");var subQ62=sQuery(id+"F0.wireOp",EDGE,"E27.3");var subQ64=sQuery(id+"F0.wireOp",EDGE,"E27.2");var subQ65=sQuery(id+"F0.wireOp",EDGE,"E27.1");var subQ66=sQuery(id+"F0.wireOp",EDGE,"E27.0");var subQ67=sQuery(id+"F0.wireOp",EDGE,"E26.5");var subQ68=sQuery(id+"F0.wireOp",EDGE,"E26.4");var subQ69=sQuery(id+"F0.wireOp",EDGE,"E26.3");var subQ70=sQuery(id+"F0.wireOp",EDGE,"E26.2");var subQ71=sQuery(id+"F0.wireOp",EDGE,"E26.1");var subQ72=sQuery(id+"F0.wireOp",EDGE,"E26.0");var subQ73=sQuery(id+"F0.wireOp",EDGE,"E21.4");var subQ74=sQuery(id+"F0.wireOp",EDGE,"E21.3");var subQ75=sQuery(id+"F0.wireOp",EDGE,"E21.2");var subQ76=sQuery(id+"F0.wireOp",EDGE,"E21.1");var subQ77=sQuery(id+"F0.wireOp",EDGE,"E21.0");var subQ78=sQuery(id+"F0.wireOp",EDGE,"E20.5");var subQ79=sQuery(id+"F0.wireOp",EDGE,"E20.4");var subQ80=sQuery(id+"F0.wireOp",EDGE,"E20.3");var subQ81=sQuery(id+"F0.wireOp",EDGE,"E20.2");var subQ82=sQuery(id+"F0.wireOp",EDGE,"E20.1");var subQ83=sQuery(id+"F0.wireOp",EDGE,"E20.0");var subQ84=sQuery(id+"F0.wireOp",EDGE,"E12");var subQ85=sQuery(id+"F0.wireOp",EDGE,"E11");var subQ86=sQuery(id+"F0.wireOp",EDGE,"E13");var subQ87=sQuery(id+"F0.wireOp",EDGE,"E21.5");var subQ88=sQuery(id+"F0.wireOp",EDGE,"E38.1");var subQ89=sQuery(id+"F0.wireOp",EDGE,"E10");var subQ90=sQuery(id+"F0.wireOp",EDGE,"E25.5");var subQ91=sQuery(id+"F0.wireOp",EDGE,"E19");var subQ92=sQuery(id+"F0.wireOp",EDGE,"E14");var subQ93=sQuery(id+"F0.wireOp",EDGE,"E15");var subQ94=sQuery(id+"F0.wireOp",EDGE,"E16");var subQ95=sQuery(id+"F0.wireOp",EDGE,"E17");var subQ96=sQuery(id+"F0.wireOp",EDGE,"E18");var subQ97=sQuery(id+"F0.wireOp",EDGE,"E22.0");var subQ98=sQuery(id+"F0.wireOp",EDGE,"E22.1");var subQ99=sQuery(id+"F0.wireOp",EDGE,"E22.2");var subQ100=sQuery(id+"F0.wireOp",EDGE,"E22.3");var subQ102=sQuery(id+"F0.wireOp",EDGE,"E22.4");var subQ112=sQuery(id+"F0.wireOp",EDGE,"E22.5");var subQ113=sQuery(id+"F0.wireOp",EDGE,"E23.0");var subQ114=sQuery(id+"F0.wireOp",EDGE,"E23.1");var subQ115=sQuery(id+"F0.wireOp",EDGE,"E23.2");var subQ116=sQuery(id+"F0.wireOp",EDGE,"E23.3");var subQ117=sQuery(id+"F0.wireOp",EDGE,"E23.4");var subQ118=sQuery(id+"F0.wireOp",EDGE,"E23.5");var subQ119=sQuery(id+"F0.wireOp",EDGE,"E24.0");var subQ120=sQuery(id+"F0.wireOp",EDGE,"E24.1");var subQ121=sQuery(id+"F0.wireOp",EDGE,"E24.2");var subQ122=sQuery(id+"F0.wireOp",EDGE,"E24.3");var subQ123=sQuery(id+"F0.wireOp",EDGE,"E24.4");var subQ124=sQuery(id+"F0.wireOp",EDGE,"E24.5");var subQ125=sQuery(id+"F0.wireOp",EDGE,"E25.0");var subQ126=sQuery(id+"F0.wireOp",EDGE,"E25.1");var subQ127=sQuery(id+"F0.wireOp",EDGE,"E25.2");var subQ128=sQuery(id+"F0.wireOp",EDGE,"E25.3");var subQ129=sQuery(id+"F0.wireOp",EDGE,"E25.4");var subQ130=sQuery(id+"F0.wireOp",EDGE,"E38.2");var subQ131=sQuery(id+"F0.wireOp",EDGE,"E39.0");var subQ133=sQuery(id+"F0.wireOp",EDGE,"E39.1");var subQ136=sQuery(id+"F0.wireOp",EDGE,"E39.2");var subQ137=sQuery(id+"F0.wireOp",EDGE,"E41.bottom");var subQ138=sQuery(id+"F0.wireOp",EDGE,"E41.top");var subQ139=sQuery(id+"F0.wireOp",EDGE,"E41.left");var subQ140=sQuery(id+"F0.wireOp",EDGE,"E41.right");var subQ141=sQuery(id+"F0.wireOp",EDGE,"E42.bottom");var subQ148=sQuery(id+"F0.wireOp",EDGE,"E42.top");var subQ149=sQuery(id+"F0.wireOp",EDGE,"E42.left");var subQ150=sQuery(id+"F0.wireOp",EDGE,"E42.right");var subQ151=sQuery(id+"F0.wireOp",EDGE,"E43.bottom");var subQ152=sQuery(id+"F0.wireOp",EDGE,"E43.top");var subQ153=sQuery(id+"F0.wireOp",EDGE,"E43.left");var subQ154=sQuery(id+"F0.wireOp",EDGE,"E43.right");var subQ155=sQuery(id+"F0.wireOp",EDGE,"E44.bottom");var subQ156=sQuery(id+"F0.wireOp",EDGE,"E44.top");var subQ157=sQuery(id+"F0.wireOp",EDGE,"E44.left");var subQ158=sQuery(id+"F0.wireOp",EDGE,"E44.right");var subQ159=sQuery(id+"F0.wireOp",EDGE,"E45.bottom");var subQ160=sQuery(id+"F0.wireOp",EDGE,"E45.top");var subQ161=sQuery(id+"F0.wireOp",EDGE,"E45.left");var subQ162=sQuery(id+"F0.wireOp",EDGE,"E45.right");var subQ163=sQuery(id+"F0.wireOp",EDGE,"E46.bottom");var subQ164=sQuery(id+"F0.wireOp",EDGE,"E46.top");var subQ165=sQuery(id+"F0.wireOp",EDGE,"E46.left");var subQ166=sQuery(id+"F0.wireOp",EDGE,"E46.right");var subQ167=sQuery(id+"F0.wireOp",EDGE,"E47.bottom");var subQ168=sQuery(id+"F0.wireOp",EDGE,"E47.top");var subQ169=sQuery(id+"F0.wireOp",EDGE,"E47.left");var subQ170=sQuery(id+"F0.wireOp",EDGE,"E47.right");var subQ171=sQuery(id+"F0.wireOp",EDGE,"E48.bottom");var subQ172=sQuery(id+"F0.wireOp",EDGE,"E48.top");var subQ173=sQuery(id+"F0.wireOp",EDGE,"E48.left");var subQ174=sQuery(id+"F0.wireOp",EDGE,"E48.right");var subQ175=sQuery(id+"F0.wireOp",EDGE,"E49.bottom");var subQ176=sQuery(id+"F0.wireOp",EDGE,"E49.top");var subQ177=sQuery(id+"F0.wireOp",EDGE,"E49.left");var subQ178=sQuery(id+"F0.wireOp",EDGE,"E49.right");var subQ179=sQuery(id+"F0.wireOp",EDGE,"E50.bottom");var subQ180=sQuery(id+"F0.wireOp",EDGE,"E50.top");var subQ181=sQuery(id+"F0.wireOp",EDGE,"E50.left");var subQ182=sQuery(id+"F0.wireOp",EDGE,"E50.right");Q0=makeQuery(id+"F3.boolean.opBoolean","SPLIT",FACE,{"disambiguationData":[TD([makeQuery(id+"F1.opExtrude","SWEPT_FACE",FACE,{"disambiguationData":[OSD([subQ89])]})])],"derivedFrom":makeQuery(id+"F1.opExtrude","CAP_FACE",FACE,{"disambiguationData":[OSD([subQ89,subQ85,subQ84,subQ86,subQ92,subQ93,subQ94,subQ95,subQ96,subQ91,subQ83,subQ82,subQ81,subQ80,subQ79,subQ78,subQ77,subQ76,subQ75,subQ74,subQ73,subQ87,subQ97,subQ98,subQ99,subQ100,subQ102,subQ112,subQ113,subQ114,subQ115,subQ116,subQ117,subQ118,subQ119,subQ120,subQ121,subQ122,subQ123,subQ124,subQ125,subQ126,subQ127,subQ128,subQ129,subQ90,subQ72,subQ71,subQ70,subQ69,subQ68,subQ67,subQ66,subQ65,subQ64,subQ62,subQ60,subQ58,subQ56,subQ54,subQ52,subQ50,subQ48,subQ46,subQ44,subQ42,subQ41,subQ39,subQ38,subQ36,subQ34,subQ32,subQ30,subQ29,subQ28,subQ26,subQ25,subQ23,subQ21,subQ19,subQ17,subQ16,subQ15,subQ14,subQ13,subQ12,subQ11,subQ10,subQ8,subQ6,subQ4,subQ3,subQ2,subQ1,subQ0,subQ88,subQ130,subQ131,subQ133,subQ136,subQ137,subQ138,subQ139,subQ140,subQ141,subQ148,subQ149,subQ150,subQ151,subQ152,subQ153,subQ154,subQ155,subQ156,subQ157,subQ158,subQ159,subQ160,subQ161,subQ162,subQ163,subQ164,subQ165,subQ166,subQ167,subQ168,subQ169,subQ170,subQ171,subQ172,subQ173,subQ174,subQ175,subQ176,subQ177,subQ178,subQ179,subQ180,subQ181,subQ182])],"isStart":false})});}
            var sketch = newSketch(context, id + "F6", { "sketchPlane" : qUnion([Q0])});
            skLineSegment(sketch, "E53.bottom", {"start": v(-1, 80.61) * mm, "end": v(-0.5, 80.61) * mm});
            skLineSegment(sketch, "E53.top", {"start": v(-1, 75.61) * mm, "end": v(-0.5, 75.61) * mm});
            skLineSegment(sketch, "E53.left", {"start": v(-1, 80.61) * mm, "end": v(-1, 75.61) * mm});
            skLineSegment(sketch, "E53.right", {"start": v(-0.5, 80.61) * mm, "end": v(-0.5, 75.61) * mm});
            skLineSegment(sketch, "E54.bottom", {"start": v(9, 80.61) * mm, "end": v(9.5, 80.61) * mm});
            skLineSegment(sketch, "E54.top", {"start": v(9, 78.11) * mm, "end": v(9.5, 78.11) * mm});
            skLineSegment(sketch, "E54.left", {"start": v(9, 80.61) * mm, "end": v(9, 78.11) * mm});
            skLineSegment(sketch, "E54.right", {"start": v(9.5, 80.61) * mm, "end": v(9.5, 78.11) * mm});
            skLineSegment(sketch, "E55.bottom", {"start": v(19, 80.61) * mm, "end": v(19.5, 80.61) * mm});
            skLineSegment(sketch, "E55.top", {"start": v(19, 78.11) * mm, "end": v(19.5, 78.11) * mm});
            skLineSegment(sketch, "E55.left", {"start": v(19, 80.61) * mm, "end": v(19, 78.11) * mm});
            skLineSegment(sketch, "E55.right", {"start": v(19.5, 80.61) * mm, "end": v(19.5, 78.11) * mm});
            skLineSegment(sketch, "E56.bottom", {"start": v(29, 80.61) * mm, "end": v(29.5, 80.61) * mm});
            skLineSegment(sketch, "E56.top", {"start": v(29, 78.11) * mm, "end": v(29.5, 78.11) * mm});
            skLineSegment(sketch, "E56.left", {"start": v(29, 80.61) * mm, "end": v(29, 78.11) * mm});
            skLineSegment(sketch, "E56.right", {"start": v(29.5, 80.61) * mm, "end": v(29.5, 78.11) * mm});
            skLineSegment(sketch, "E57.bottom", {"start": v(39, 80.61) * mm, "end": v(39.5, 80.61) * mm});
            skLineSegment(sketch, "E57.top", {"start": v(39, 78.11) * mm, "end": v(39.5, 78.11) * mm});
            skLineSegment(sketch, "E57.left", {"start": v(39, 80.61) * mm, "end": v(39, 78.11) * mm});
            skLineSegment(sketch, "E57.right", {"start": v(39.5, 80.61) * mm, "end": v(39.5, 78.11) * mm});
            skLineSegment(sketch, "E58.bottom", {"start": v(49, 80.61) * mm, "end": v(49.5, 80.61) * mm});
            skLineSegment(sketch, "E58.top", {"start": v(49, 75.61) * mm, "end": v(49.5, 75.61) * mm});
            skLineSegment(sketch, "E58.left", {"start": v(49, 80.61) * mm, "end": v(49, 75.61) * mm});
            skLineSegment(sketch, "E58.right", {"start": v(49.5, 80.61) * mm, "end": v(49.5, 75.61) * mm});
            skLineSegment(sketch, "E59.bottom", {"start": v(59, 80.61) * mm, "end": v(59.5, 80.61) * mm});
            skLineSegment(sketch, "E59.top", {"start": v(59, 78.11) * mm, "end": v(59.5, 78.11) * mm});
            skLineSegment(sketch, "E59.left", {"start": v(59, 80.61) * mm, "end": v(59, 78.11) * mm});
            skLineSegment(sketch, "E59.right", {"start": v(59.5, 80.61) * mm, "end": v(59.5, 78.11) * mm});
            skLineSegment(sketch, "E60.bottom", {"start": v(69, 80.61) * mm, "end": v(69.5, 80.61) * mm});
            skLineSegment(sketch, "E60.top", {"start": v(69, 78.11) * mm, "end": v(69.5, 78.11) * mm});
            skLineSegment(sketch, "E60.left", {"start": v(69, 80.61) * mm, "end": v(69, 78.11) * mm});
            skLineSegment(sketch, "E60.right", {"start": v(69.5, 80.61) * mm, "end": v(69.5, 78.11) * mm});
            skLineSegment(sketch, "E61.bottom", {"start": v(79, 80.61) * mm, "end": v(79.5, 80.61) * mm});
            skLineSegment(sketch, "E61.top", {"start": v(79, 78.11) * mm, "end": v(79.5, 78.11) * mm});
            skLineSegment(sketch, "E61.left", {"start": v(79, 80.61) * mm, "end": v(79, 78.11) * mm});
            skLineSegment(sketch, "E61.right", {"start": v(79.5, 80.61) * mm, "end": v(79.5, 78.11) * mm});
            skLineSegment(sketch, "E62.bottom", {"start": v(89, 80.61) * mm, "end": v(89.5, 80.61) * mm});
            skLineSegment(sketch, "E62.top", {"start": v(89, 78.11) * mm, "end": v(89.5, 78.11) * mm});
            skLineSegment(sketch, "E62.left", {"start": v(89, 80.61) * mm, "end": v(89, 78.11) * mm});
            skLineSegment(sketch, "E62.right", {"start": v(89.5, 80.61) * mm, "end": v(89.5, 78.11) * mm});
            skLineSegment(sketch, "E63.bottom", {"start": v(99, 80.61) * mm, "end": v(99.5, 80.61) * mm});
            skLineSegment(sketch, "E63.top", {"start": v(99, 75.61) * mm, "end": v(99.5, 75.61) * mm});
            skLineSegment(sketch, "E63.left", {"start": v(99, 80.61) * mm, "end": v(99, 75.61) * mm});
            skLineSegment(sketch, "E63.right", {"start": v(99.5, 80.61) * mm, "end": v(99.5, 75.61) * mm});
            skLineSegment(sketch, "E64.bottom", {"start": v(109, 80.61) * mm, "end": v(109.5, 80.61) * mm});
            skLineSegment(sketch, "E64.top", {"start": v(109, 78.11) * mm, "end": v(109.5, 78.11) * mm});
            skLineSegment(sketch, "E64.left", {"start": v(109, 80.61) * mm, "end": v(109, 78.11) * mm});
            skLineSegment(sketch, "E64.right", {"start": v(109.5, 80.61) * mm, "end": v(109.5, 78.11) * mm});
            skLineSegment(sketch, "E65.bottom", {"start": v(119, 80.61) * mm, "end": v(119.5, 80.61) * mm});
            skLineSegment(sketch, "E65.top", {"start": v(119, 78.11) * mm, "end": v(119.5, 78.11) * mm});
            skLineSegment(sketch, "E65.left", {"start": v(119, 80.61) * mm, "end": v(119, 78.11) * mm});
            skLineSegment(sketch, "E65.right", {"start": v(119.5, 80.61) * mm, "end": v(119.5, 78.11) * mm});
            skLineSegment(sketch, "E66.bottom", {"start": v(129, 80.61) * mm, "end": v(129.5, 80.61) * mm});
            skLineSegment(sketch, "E66.top", {"start": v(129, 78.11) * mm, "end": v(129.5, 78.11) * mm});
            skLineSegment(sketch, "E66.left", {"start": v(129, 80.61) * mm, "end": v(129, 78.11) * mm});
            skLineSegment(sketch, "E66.right", {"start": v(129.5, 80.61) * mm, "end": v(129.5, 78.11) * mm});
            skLineSegment(sketch, "E67.bottom", {"start": v(139, 80.61) * mm, "end": v(139.5, 80.61) * mm});
            skLineSegment(sketch, "E67.top", {"start": v(139, 78.11) * mm, "end": v(139.5, 78.11) * mm});
            skLineSegment(sketch, "E67.left", {"start": v(139, 80.61) * mm, "end": v(139, 78.11) * mm});
            skLineSegment(sketch, "E67.right", {"start": v(139.5, 80.61) * mm, "end": v(139.5, 78.11) * mm});
            skLineSegment(sketch, "E68.bottom", {"start": v(149, 80.61) * mm, "end": v(149.5, 80.61) * mm});
            skLineSegment(sketch, "E68.top", {"start": v(149, 75.61) * mm, "end": v(149.5, 75.61) * mm});
            skLineSegment(sketch, "E68.left", {"start": v(149, 80.61) * mm, "end": v(149, 75.61) * mm});
            skLineSegment(sketch, "E68.right", {"start": v(149.5, 80.61) * mm, "end": v(149.5, 75.61) * mm});
            skLineSegment(sketch, "E69.bottom", {"start": v(159.5, 80.61) * mm, "end": v(160, 80.61) * mm});
            skLineSegment(sketch, "E69.top", {"start": v(159.5, 78.11) * mm, "end": v(160, 78.11) * mm});
            skLineSegment(sketch, "E69.left", {"start": v(159.5, 80.61) * mm, "end": v(159.5, 78.11) * mm});
            skLineSegment(sketch, "E69.right", {"start": v(160, 80.61) * mm, "end": v(160, 78.11) * mm});
            skLineSegment(sketch, "E70.bottom", {"start": v(169.5, 80.61) * mm, "end": v(170, 80.61) * mm});
            skLineSegment(sketch, "E70.top", {"start": v(169.5, 78.11) * mm, "end": v(170, 78.11) * mm});
            skLineSegment(sketch, "E70.left", {"start": v(169.5, 80.61) * mm, "end": v(169.5, 78.11) * mm});
            skLineSegment(sketch, "E70.right", {"start": v(170, 80.61) * mm, "end": v(170, 78.11) * mm});
            skLineSegment(sketch, "E71.bottom", {"start": v(179.5, 80.61) * mm, "end": v(180, 80.61) * mm});
            skLineSegment(sketch, "E71.top", {"start": v(179.5, 78.11) * mm, "end": v(180, 78.11) * mm});
            skLineSegment(sketch, "E71.left", {"start": v(179.5, 80.61) * mm, "end": v(179.5, 78.11) * mm});
            skLineSegment(sketch, "E71.right", {"start": v(180, 80.61) * mm, "end": v(180, 78.11) * mm});
            skLineSegment(sketch, "E72.bottom", {"start": v(190, 80.61) * mm, "end": v(190.5, 80.61) * mm});
            skLineSegment(sketch, "E72.top", {"start": v(190, 78.11) * mm, "end": v(190.5, 78.11) * mm});
            skLineSegment(sketch, "E72.left", {"start": v(190, 80.61) * mm, "end": v(190, 78.11) * mm});
            skLineSegment(sketch, "E72.right", {"start": v(190.5, 80.61) * mm, "end": v(190.5, 78.11) * mm});
            skLineSegment(sketch, "E73.bottom", {"start": v(200, 80.61) * mm, "end": v(200.5, 80.61) * mm});
            skLineSegment(sketch, "E73.top", {"start": v(200, 75.61) * mm, "end": v(200.5, 75.61) * mm});
            skLineSegment(sketch, "E73.left", {"start": v(200, 80.61) * mm, "end": v(200, 75.61) * mm});
            skLineSegment(sketch, "E73.right", {"start": v(200.5, 80.61) * mm, "end": v(200.5, 75.61) * mm});
            skLineSegment(sketch, "E74", {"start": v(-6, 70.61) * mm, "end": v(205, 70.61) * mm});
            skText(sketch, "E75", { "text": "0", "fontName": "OpenSans-Bold.ttf"});
            skText(sketch, "E76", { "text": "5", "fontName": "OpenSans-Bold.ttf"});
            skText(sketch, "E77", { "text": "10", "fontName": "OpenSans-Regular.ttf"});
            skText(sketch, "E78", { "text": "15", "fontName": "OpenSans-Bold.ttf"});
            skText(sketch, "E79", { "text": "20", "fontName": "OpenSans-Bold.ttf"});
            const initialGuessF6  = {"E75": [-0.002, 0.07061, 1, 0, 0.003], "E76": [0.048, 0.07061, 1, 0, 0.003], "E77": [0.0965, 0.07061, 1, 0, 0.003], "E78": [0.1465, 0.07061, 1, 0, 0.003], "E79": [0.1975, 0.07061, 1, 0, 0.003]};
            skSetInitialGuess(sketch, initialGuessF6);
            skSolve(sketch);
        }
        {
            var Q0;
            Q0 = qSketchRegion(id + "F6", true);
            extrude(context, id + "F7", {"entities" : qUnion([Q0]), "operationType" : NewBodyOperationType.ADD, "depth" : .5 * mm, "offsetDistance" : 25 * mm});
        }
    });
